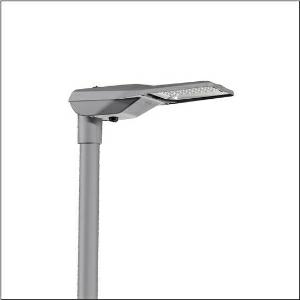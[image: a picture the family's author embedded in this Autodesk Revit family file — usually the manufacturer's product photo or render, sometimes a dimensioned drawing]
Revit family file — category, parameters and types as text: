
# Revit family: streetlight_sl_21_mini___st0_8a_5xe2c63t08hb_8657
name_source: partatom
category: Lighting Fixtures
units: mm (PartAtom-declared; Revit-internal decimal feet)

## family parameters
Cut with Voids When Loaded = No
Host = Face
Light Source = No
Part Type = Normal
Room Calculation Point = No
Round Connector Dimension = Use Diameter
Shared = No

## types (1)
- --- (1 x LED, 8110 lm, 66 W, 2700K)
    Apparent Load = 66 VA
    CIE Flux Codes = 38 75 97 100 100
    Color Rendering = 70
    Color Temperature = 2700K
    Default Elevation = 1800 mm
    Description = Streetlight SL 21 mini, mast luminaire, primary light control with lens, of PMMA, primary optical cover: cover, of toughened safety glass, transparent, light distribution: ST0.8a, light emission: direct distribution, primary light characteristic: asymmetric, installation type: side-entry, post-top, LED, High Power LED, rated luminous flux: 8.110lm, luminous efficacy: 123lm/W, light colour: 727, colour temperature: 2700K, control gear: D4i, control: overheat protection, constant luminous flux control, time-dependent luminous flux control, flexible luminous flux parameterisation, pre-setting: logarithmic dimming characteristic, mains connection: 220..240V, AC, 50/60Hz, start of lifetime: 66W, end of service life: 69W, reduction: 30W, luminaire housing, of diecast aluminium, powder-coated, Siteco® metallic grey (DB 702S), corrosivity category C5 mid according to DIN EN ISO 12944, please order mast flange separately, inclination adjustable: 0°, 5°, 10°, 15°, sealing non-destructively replaceable, multi-level sealing system, length: 628mm, width: 235mm, height: 110mm, mast flange for spigot size: 42mm (side-entry): 5XC10008XM4, 60/48mm (side-entry/post-top): 5XC10108XM2, 76/60mm (side-entry/post-top): 5XC10108XM1, mounting height: 4..8m, Smart Interface below and above, protection rating (complete): IP66, insulation class (complete): insulation class II (safety insulation), certification: CE, ENEC, ENEC+, VDE, impact resistance: IK10, permissible operating ambient temperature for outdoor applications: -40..+50°C, standard-compliant lighting for roads and squares, packaging unit: 1 piece

Light Distribution: ST0.8a
    Height = 110 mm
    Lamp = 1 x LED
    Lamp Light Flux = 8110 lm
    Lamp Power = 66 W
    Lamp count = 1
    Length = 625 mm
    Luminous efficacy = 123 lm/W
    Manufacturer = Siteco
    ModVariant = No
    Model = 5XE2C63T08HB
    Number of Poles = 1
    OnlyDefault = Yes
    Power Factor = 1
    Product Name = Streetlight SL 21 mini | ST0.8a
    Product group = mast luminaire | pylon top
    ProductGroupID = 6100
    Protection Class = Protection class II
    Protection Degree = IP 66
    RLX_Detail_Level = 1
    RLX_Emergency_Light_Flux = 0 lm
    RLX_Emergency_Type = 0
    RLX_Emergency_Type_DB = No
    RlxData = <blob elided: 26361 chars, md5=6f6e9190>
    Socket = socket
    Standby Power = 0 W
    System Light Flux = 8110 lm
    System Power = 66 W
    Type Comments = factory setting: luminous flux: 100 % | dim-lin: 254 | 670 mA
    Type Image = l_1003514.jpg
    URL = http://relux.com
    VarID = @adj_185234
    Voltage = 0 V
    Weight = 0.00 kg
    Width = 234 mm

## geometry (parser evidence)
native form markers: Blend x4, Sweep x9
no freeform markers — native parametric forms only
